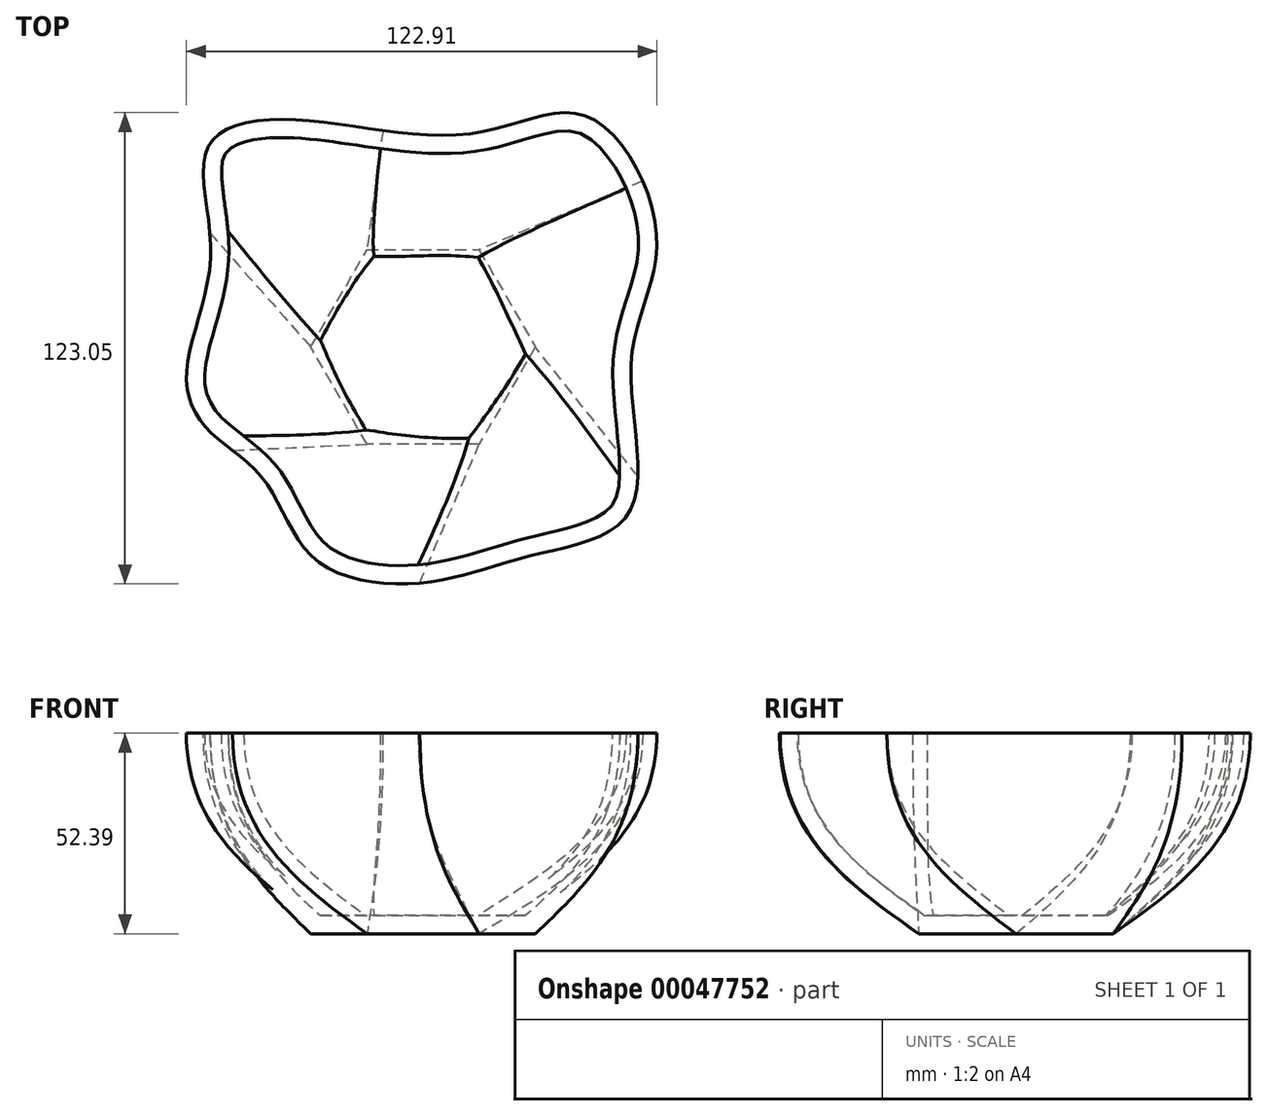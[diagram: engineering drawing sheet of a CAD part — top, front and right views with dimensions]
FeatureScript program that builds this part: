
annotation { "Feature Type Name" : "Feature", "Feature Type Description" : "" }
export const myFeature = defineFeature(function(context is Context, id is Id, definition is map)
    precondition{}
    {
        {
            var Q0;
            Q0=qCreatedBy(makeId("Top.planeOp"),FACE);
            var sketch = newSketch(context, id + "F0", { "sketchPlane" : qUnion([Q0])});
            skCircle(sketch, "E0.cCircle", {"center": v(0, 0) * mm, "radius": 25.4 * mm, "construction": true});
            skLineSegment(sketch, "E0.0", {"start": v(-14.66, 25.4) * mm, "end": v(14.66, 25.4) * mm});
            skLineSegment(sketch, "E0.1", {"start": v(14.66, 25.4) * mm, "end": v(29.33, 0) * mm});
            skLineSegment(sketch, "E0.2", {"start": v(29.33, 0) * mm, "end": v(14.66, -25.4) * mm});
            skLineSegment(sketch, "E0.3", {"start": v(14.66, -25.4) * mm, "end": v(-14.66, -25.4) * mm});
            skLineSegment(sketch, "E0.4", {"start": v(-14.66, -25.4) * mm, "end": v(-29.33, 0) * mm});
            skLineSegment(sketch, "E0.5", {"start": v(-29.33, 0) * mm, "end": v(-14.66, 25.4) * mm});
            skPoint(sketch, "E0.0.midPoint", {"position": v(0, 25.4) * mm});
            skSolve(sketch);
        }
        {
            var Q0;
            Q0=qCreatedBy(makeId("Top.planeOp"),FACE);
            cPlane(context, id + "F1", {"entities" : qUnion([Q0]), "cplaneType" : CPlaneType.OFFSET, "offset" : 52.4 * mm, "width" : 152.4 * mm, "height" : 152.4 * mm});
        }
        {
            var Q0;
            Q0=qCreatedBy(id+"F1.planeOp",FACE);
            var sketch = newSketch(context, id + "F2", { "sketchPlane" : qUnion([Q0])});
            skLineSegment(sketch, "E1.rect.bottom", {"start": v(-65.09, 65.09) * mm, "end": v(65.09, 65.09) * mm, "construction": true});
            skLineSegment(sketch, "E1.rect.top", {"start": v(-65.09, -65.09) * mm, "end": v(65.09, -65.09) * mm, "construction": true});
            skLineSegment(sketch, "E1.rect.left", {"start": v(-65.09, 65.09) * mm, "end": v(-65.09, -65.09) * mm, "construction": true});
            skLineSegment(sketch, "E1.rect.right", {"start": v(65.09, 65.09) * mm, "end": v(65.09, -65.09) * mm, "construction": true});
            skPoint(sketch, "E1.rect.middle", {"position": v(0, 0) * mm});
            skPoint(sketch, "E2.rect.middle", {"position": v(-59.93, 65.09) * mm});
            skFitSpline(sketch, "E3", {"points": [v(0, -61.57) * mm, v(-28.31, -55.32) * mm, v(-41.55, -34.73) * mm, v(-56.62, -21.12) * mm, v(-61.77, -6.05) * mm, v(-55.52, 23.74) * mm, v(-56.25, 52.05) * mm, v(-34.93, 59.4) * mm, v(12.87, 55.73) * mm, v(43.02, 60.14) * mm, v(61.04, 28.52) * mm, v(54.42, -3.47) * mm, v(54.05, -42.81) * mm, v(27.95, -54.58) * mm, v(0, -61.57) * mm]});
            skSolve(sketch);
        }
        {
            var Q0;
            Q0=makeQuery(id+"F2.imprint","IMPRINT",FACE,{"disambiguationData":[TD([[makeQuery(id+"F2.imprint","IMPRINT",EDGE,{"derivedFrom":sQuery(id+"F2.wireOp",EDGE,"E3")}),-1.0]])]});
            var Q1;
            Q1=makeQuery(id+"F0.imprint","IMPRINT",FACE,{"disambiguationData":[TD([[makeQuery(id+"F0.imprint","IMPRINT",EDGE,{"derivedFrom":sQuery(id+"F0.wireOp",EDGE,"E0.0")}),-1.0]])]});
            loft(context, id + "F3", {"startCondition" : LoftEndDerivativeType.NORMAL_TO_PROFILE, "startMagnitude" : 1.5, "sheetProfilesArray" : [{ "sheetProfileEntities" : qUnion([Q0]) }, { "sheetProfileEntities" : qUnion([Q1]) }]});
        }
        {
            var Q0;
            Q0=makeQuery(id+"F3.opLoft","CAP_FACE",FACE,{"disambiguationData":[OSD([makeQuery(id+"F2.imprint","IMPRINT",FACE,{"disambiguationData":[TD([[makeQuery(id+"F2.imprint","IMPRINT",EDGE,{"derivedFrom":sQuery(id+"F2.wireOp",EDGE,"E3")}),-1.0]])]})])],"isStart":true});
            shell(context, id + "F4", {"entities" : qUnion([Q0]), "thickness" : 4.76 * mm});
        }
    });
